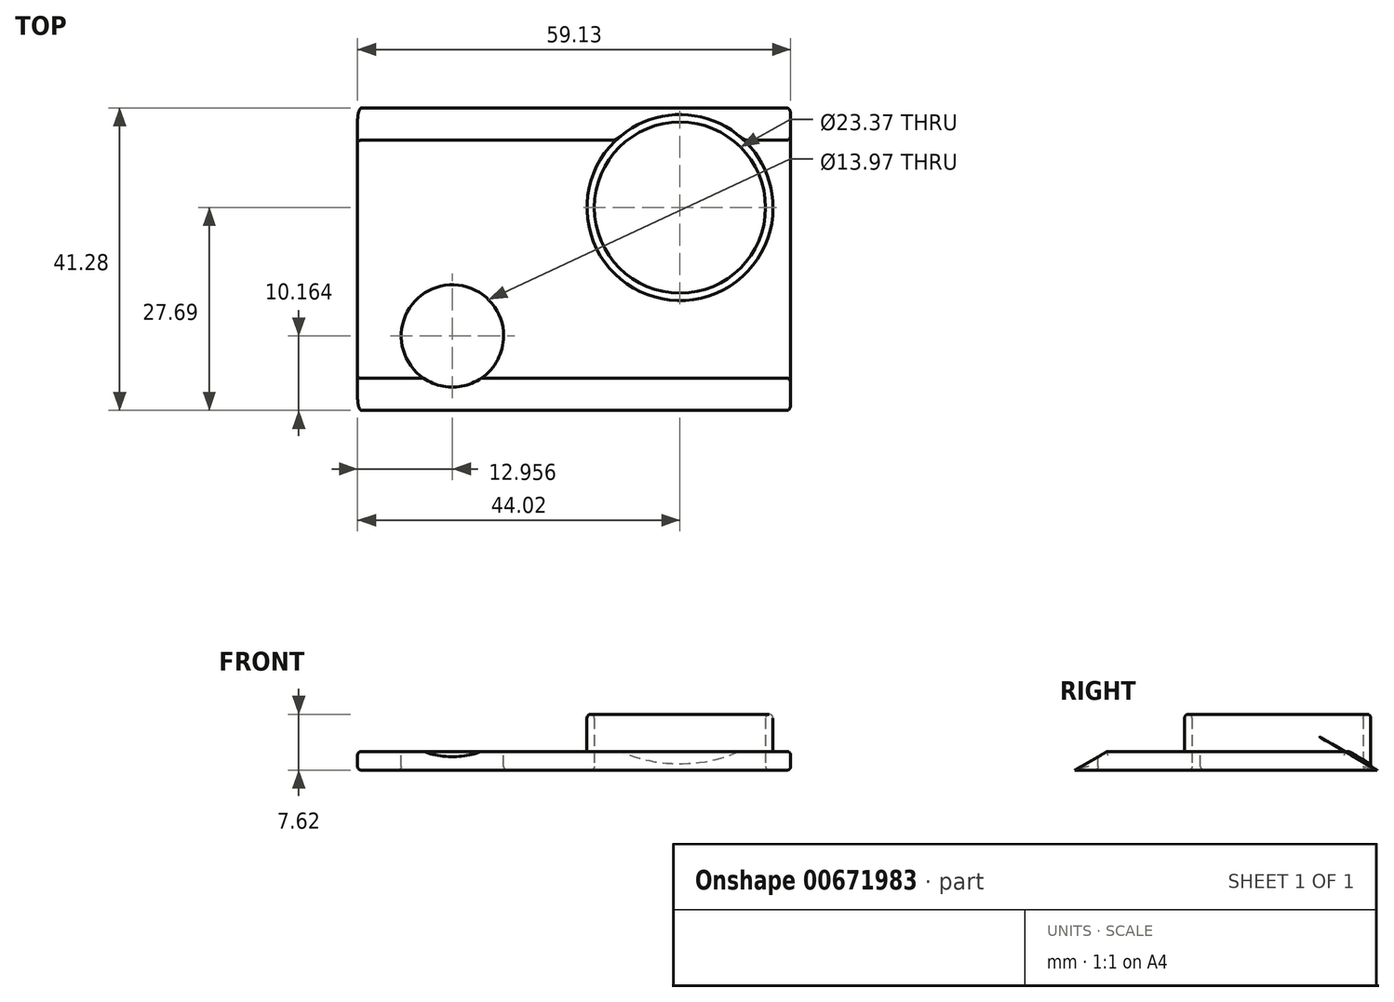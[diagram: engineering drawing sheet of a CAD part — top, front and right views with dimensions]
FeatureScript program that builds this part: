
annotation { "Feature Type Name" : "Feature", "Feature Type Description" : "" }
export const myFeature = defineFeature(function(context is Context, id is Id, definition is map)
    precondition{}
    {
        {
            var Q0;
            Q0=qCreatedBy(makeId("Top.planeOp"),FACE);
            var sketch = newSketch(context, id + "F0", { "sketchPlane" : qUnion([Q0])});
            skCircle(sketch, "E0", {"center": v(0, 0) * mm, "radius": 11.68 * mm});
            skCircle(sketch, "E1", {"center": v(0, 0) * mm, "radius": 12.7 * mm});
            skSolve(sketch);
        }
        {
            var Q0;
            Q0 = qSketchRegion(id + "F0", true);
            extrude(context, id + "F1", {"entities" : qUnion([Q0]), "depth" : 7.62 * mm, "offsetDistance" : 25.4 * mm});
        }
        {
            var Q0;
            Q0=makeQuery(id+"F1.opExtrude","CAP_FACE",FACE,{"disambiguationData":[OSD([sQuery(id+"F0.wireOp",EDGE,"E0"),sQuery(id+"F0.wireOp",EDGE,"E1")])],"isStart":true});
            var sketch = newSketch(context, id + "F2", { "sketchPlane" : qUnion([Q0])});
            skLineSegment(sketch, "E2.bottom", {"start": v(-44.02, -13.59) * mm, "end": v(15.11, -13.59) * mm});
            skLineSegment(sketch, "E2.top", {"start": v(-44.02, 27.69) * mm, "end": v(15.11, 27.69) * mm});
            skLineSegment(sketch, "E2.left", {"start": v(-44.02, -13.59) * mm, "end": v(-44.02, 27.69) * mm});
            skLineSegment(sketch, "E2.right", {"start": v(15.11, -13.59) * mm, "end": v(15.11, 27.69) * mm});
            skCircle(sketch, "E3.0", {"center": v(0, 0) * mm, "radius": 11.68 * mm});
            skSolve(sketch);
        }
        {
            var Q0;
            Q0 = qSketchRegion(id + "F2", true);
            extrude(context, id + "F3", {"entities" : qUnion([Q0]), "operationType" : NewBodyOperationType.ADD, "oppositeDirection" : true, "depth" : 2.54 * mm, "offsetDistance" : 25.4 * mm});
        }
        {
            var Q0;
            Q0=makeQuery(id+"F3.opExtrude","SWEPT_FACE",FACE,{"disambiguationData":[OSD([sQuery(id+"F2.wireOp",EDGE,"E2.right")])]});
            var sketch = newSketch(context, id + "F4", { "sketchPlane" : qUnion([Q0])});
            skLineSegment(sketch, "E4", {"start": v(-23.29, 2.54) * mm, "end": v(-27.69, 0) * mm});
            skLineSegment(sketch, "E5", {"start": v(-23.29, 2.54) * mm, "end": v(-27.69, 2.54) * mm});
            skLineSegment(sketch, "E6", {"start": v(-27.69, 0) * mm, "end": v(-27.69, 2.54) * mm});
            skLineSegment(sketch, "E7", {"start": v(9.19, 2.54) * mm, "end": v(13.59, 0) * mm});
            skLineSegment(sketch, "E8", {"start": v(9.19, 2.54) * mm, "end": v(13.59, 2.54) * mm});
            skLineSegment(sketch, "E9", {"start": v(13.59, 0) * mm, "end": v(13.59, 2.54) * mm});
            skSolve(sketch);
        }
        {
            var Q0;
            Q0 = qSketchRegion(id + "F4", true);
            extrude(context, id + "F5", {"entities" : qUnion([Q0]), "operationType" : NewBodyOperationType.REMOVE, "endBound" : BoundingType.THROUGH_ALL, "oppositeDirection" : true, "depth" : 25.4 * mm, "offsetDistance" : 25.4 * mm});
        }
        {
            var Q0;
            Q0=makeQuery(id+"F5.boolean.opBoolean","COPY",FACE,{"derivedFrom":makeQuery(id+"F5.opExtrude","SWEPT_FACE",FACE,{"disambiguationData":[OSD([sQuery(id+"F4.wireOp",EDGE,"E8")])]})});
            var sketch = newSketch(context, id + "F6", { "sketchPlane" : qUnion([Q0])});
            skArc(sketch, "E10.0", {"start": v(-8.77, -9.19) * mm, "mid": v(0, -12.7) * mm, "end": v(8.77, -9.19) * mm});
            skArc(sketch, "E10.1", {"start": v(7.22, -9.19) * mm, "mid": v(0, -11.68) * mm, "end": v(-7.22, -9.19) * mm});
            skLineSegment(sketch, "E10.2", {"start": v(7.22, -9.19) * mm, "end": v(8.77, -9.19) * mm});
            skLineSegment(sketch, "E10.3", {"start": v(-8.77, -9.19) * mm, "end": v(-7.22, -9.19) * mm});
            skSolve(sketch);
        }
        {
            var Q0;
            Q0 = qSketchRegion(id + "F6", true);
            var Q1;
            Q1=makeQuery(id+"F3.boolean.opBoolean","MERGE",FACE,{"derivedFrom":[makeQuery(id+"F1.opExtrude","CAP_FACE",FACE,{"disambiguationData":[OSD([sQuery(id+"F0.wireOp",EDGE,"E0"),sQuery(id+"F0.wireOp",EDGE,"E1")])],"isStart":true}),makeQuery(id+"F3.opExtrude","CAP_FACE",FACE,{"disambiguationData":[OSD([sQuery(id+"F2.wireOp",EDGE,"E2.bottom"),sQuery(id+"F2.wireOp",EDGE,"E2.top"),sQuery(id+"F2.wireOp",EDGE,"E2.left"),sQuery(id+"F2.wireOp",EDGE,"E2.right"),sQuery(id+"F2.wireOp",EDGE,"E3.0")])],"isStart":true})]});
            extrude(context, id + "F7", {"entities" : qUnion([Q0]), "operationType" : NewBodyOperationType.ADD, "endBound" : BoundingType.UP_TO_SURFACE, "depth" : 25.4 * mm, "endBoundEntityFace" : qUnion([Q1]), "offsetDistance" : 25.4 * mm});
        }
        {
            var Q0;
            Q0=makeQuery(id+"F3.opExtrude","CAP_EDGE",EDGE,{"disambiguationData":[OSD([sQuery(id+"F2.wireOp",EDGE,"E2.right")])],"isStart":false});
            var Q1;
            {var subQ0=sQuery(id+"F4.wireOp",EDGE,"E7");var subQ1=makeQuery(id+"F5.opExtrude","SWEPT_FACE",FACE,{"disambiguationData":[OSD([subQ0])]});var subQ2=sQuery(id+"F2.wireOp",EDGE,"E2.right");var subQ3=makeQuery(id+"F3.opExtrude","CAP_FACE",FACE,{"disambiguationData":[OSD([sQuery(id+"F2.wireOp",EDGE,"E2.bottom"),sQuery(id+"F2.wireOp",EDGE,"E2.top"),sQuery(id+"F2.wireOp",EDGE,"E2.left"),subQ2,sQuery(id+"F2.wireOp",EDGE,"E3.0")])],"isStart":false});var subQ4=sQuery(id+"F4.wireOp",EDGE,"E8");Q1=makeQuery(id+"F5.boolean.opBoolean","COPY",EDGE,{"disambiguationData":[topologyDisambiguationEdgeConnected([subQ3,subQ1]),TD([makeQuery(id+"F3.opExtrude","SWEPT_FACE",FACE,{"disambiguationData":[OSD([subQ2])]})])],"derivedFrom":makeQuery(id+"F5.opExtrude","SWEPT_EDGE",EDGE,{"disambiguationData":[OSD([subQ2,subQ0,subQ4])]})});}
            var Q2;
            Q2=makeQuery(id+"F7.boolean.opBoolean","INTERSECT",EDGE,{"derivedFrom":[makeQuery(id+"F5.boolean.opBoolean","COPY",FACE,{"derivedFrom":makeQuery(id+"F5.opExtrude","SWEPT_FACE",FACE,{"disambiguationData":[OSD([sQuery(id+"F4.wireOp",EDGE,"E7")])]})}),makeQuery(id+"F7.opExtrude","SWEPT_FACE",FACE,{"disambiguationData":[OSD([sQuery(id+"F6.wireOp",EDGE,"E10.0")])]})]});
            var Q3;
            {var subQ0=sQuery(id+"F4.wireOp",EDGE,"E7");var subQ1=makeQuery(id+"F5.opExtrude","SWEPT_FACE",FACE,{"disambiguationData":[OSD([subQ0])]});var subQ2=sQuery(id+"F2.wireOp",EDGE,"E2.left");var subQ3=sQuery(id+"F2.wireOp",EDGE,"E2.right");var subQ4=makeQuery(id+"F3.opExtrude","CAP_FACE",FACE,{"disambiguationData":[OSD([sQuery(id+"F2.wireOp",EDGE,"E2.bottom"),sQuery(id+"F2.wireOp",EDGE,"E2.top"),subQ2,subQ3,sQuery(id+"F2.wireOp",EDGE,"E3.0")])],"isStart":false});var subQ5=sQuery(id+"F4.wireOp",EDGE,"E8");Q3=makeQuery(id+"F5.boolean.opBoolean","COPY",EDGE,{"disambiguationData":[topologyDisambiguationEdgeConnected([subQ4,subQ1]),TD([makeQuery(id+"F3.opExtrude","SWEPT_FACE",FACE,{"disambiguationData":[OSD([subQ2])]})])],"derivedFrom":makeQuery(id+"F5.opExtrude","SWEPT_EDGE",EDGE,{"disambiguationData":[OSD([subQ3,subQ0,subQ5])]})});}
            var Q4;
            Q4=makeQuery(id+"F1.opExtrude","CAP_EDGE",EDGE,{"disambiguationData":[OSD([sQuery(id+"F0.wireOp",EDGE,"E1")])],"isStart":false});
            var Q5;
            Q5=makeQuery(id+"F1.opExtrude","CAP_EDGE",EDGE,{"disambiguationData":[OSD([sQuery(id+"F0.wireOp",EDGE,"E0")])],"isStart":false});
            var Q6;
            Q6=makeQuery(id+"F1.opExtrude","CAP_EDGE",EDGE,{"disambiguationData":[OSD([sQuery(id+"F0.wireOp",EDGE,"E0")])],"isStart":true});
            var Q7;
            Q7=makeQuery(id+"F5.boolean.opBoolean","COPY",EDGE,{"derivedFrom":makeQuery(id+"F5.opExtrude","CAP_EDGE",EDGE,{"disambiguationData":[OSD([sQuery(id+"F4.wireOp",EDGE,"E7")])],"isStart":true})});
            var Q8;
            Q8=makeQuery(id+"F3.opExtrude","CAP_EDGE",EDGE,{"disambiguationData":[OSD([sQuery(id+"F2.wireOp",EDGE,"E2.right")])],"isStart":true});
            var Q9;
            Q9=makeQuery(id+"F5.boolean.opBoolean","COPY",EDGE,{"derivedFrom":makeQuery(id+"F5.opExtrude","SWEPT_EDGE",EDGE,{"disambiguationData":[OSD([sQuery(id+"F2.wireOp",EDGE,"E2.right"),sQuery(id+"F4.wireOp",EDGE,"E4"),sQuery(id+"F4.wireOp",EDGE,"E5")])]})});
            var Q10;
            Q10=makeQuery(id+"F5.boolean.opBoolean","INTERSECT",EDGE,{"derivedFrom":[makeQuery(id+"F3.opExtrude","SWEPT_FACE",FACE,{"disambiguationData":[OSD([sQuery(id+"F2.wireOp",EDGE,"E2.left")])]}),makeQuery(id+"F5.opExtrude","SWEPT_FACE",FACE,{"disambiguationData":[OSD([sQuery(id+"F4.wireOp",EDGE,"E4")])]})]});
            var Q11;
            Q11=makeQuery(id+"F3.opExtrude","CAP_EDGE",EDGE,{"disambiguationData":[OSD([sQuery(id+"F2.wireOp",EDGE,"E2.left")])],"isStart":false});
            var Q12;
            Q12=makeQuery(id+"F5.boolean.opBoolean","INTERSECT",EDGE,{"derivedFrom":[makeQuery(id+"F3.opExtrude","SWEPT_FACE",FACE,{"disambiguationData":[OSD([sQuery(id+"F2.wireOp",EDGE,"E2.left")])]}),makeQuery(id+"F5.opExtrude","SWEPT_FACE",FACE,{"disambiguationData":[OSD([sQuery(id+"F4.wireOp",EDGE,"E7")])]})]});
            var Q13;
            Q13=makeQuery(id+"F3.opExtrude","CAP_EDGE",EDGE,{"disambiguationData":[OSD([sQuery(id+"F2.wireOp",EDGE,"E2.left")])],"isStart":true});
            var Q14;
            Q14=makeQuery(id+"F5.boolean.opBoolean","COPY",EDGE,{"derivedFrom":makeQuery(id+"F5.opExtrude","CAP_EDGE",EDGE,{"disambiguationData":[OSD([sQuery(id+"F4.wireOp",EDGE,"E4")])],"isStart":true})});
            fillet(context, id + "F8", {"entities" : qUnion([Q0, Q1, Q2, Q3, Q4, Q5, Q6, Q7, Q8, Q9, Q10, Q11, Q12, Q13, Q14]), "radius" : 0.5 * mm, "tangentPropagation" : true, "allowEdgeOverflow" : false});
        }
        {
            var Q0;
            Q0=makeQuery(id+"F3.opExtrude","CAP_FACE",FACE,{"disambiguationData":[OSD([sQuery(id+"F2.wireOp",EDGE,"E2.bottom"),sQuery(id+"F2.wireOp",EDGE,"E2.top"),sQuery(id+"F2.wireOp",EDGE,"E2.left"),sQuery(id+"F2.wireOp",EDGE,"E2.right"),sQuery(id+"F2.wireOp",EDGE,"E3.0")])],"isStart":false});
            var sketch = newSketch(context, id + "F9", { "sketchPlane" : qUnion([Q0])});
            skCircle(sketch, "E11", {"center": v(-31.06, -17.53) * mm, "radius": 6.99 * mm});
            skSolve(sketch);
        }
        {
            var Q0;
            Q0 = qSketchRegion(id + "F9", true);
            extrude(context, id + "F10", {"entities" : qUnion([Q0]), "operationType" : NewBodyOperationType.REMOVE, "oppositeDirection" : true, "depth" : 25.4 * mm, "offsetDistance" : 25.4 * mm});
        }
        {
            var Q0;
            {var subQ0=sQuery(id+"F4.wireOp",EDGE,"E5");var subQ1=sQuery(id+"F4.wireOp",EDGE,"E4");var subQ2=sQuery(id+"F2.wireOp",EDGE,"E2.right");Q0=makeQuery(id+"F10.boolean.opBoolean","INTERSECT",EDGE,{"disambiguationData":[OD(1.0)],"derivedFrom":[makeQuery(id+"F8.opFillet","BLEND_FACE",FACE,{"disambiguationData":[OSD([subQ2,subQ1,subQ0]),TDD([makeQuery(id+"F5.boolean.opBoolean","COPY",EDGE,{"derivedFrom":makeQuery(id+"F5.opExtrude","SWEPT_EDGE",EDGE,{"disambiguationData":[OSD([subQ2,subQ1,subQ0])]})})])]}),makeQuery(id+"F10.opExtrude","SWEPT_FACE",FACE,{"disambiguationData":[OSD([sQuery(id+"F9.wireOp",EDGE,"E11")])]})]});}
            var Q1;
            Q1=makeQuery(id+"F10.boolean.opBoolean","INTERSECT",EDGE,{"derivedFrom":[makeQuery(id+"F3.boolean.opBoolean","MERGE",FACE,{"derivedFrom":[makeQuery(id+"F1.opExtrude","CAP_FACE",FACE,{"disambiguationData":[OSD([sQuery(id+"F0.wireOp",EDGE,"E0"),sQuery(id+"F0.wireOp",EDGE,"E1")])],"isStart":true}),makeQuery(id+"F3.opExtrude","CAP_FACE",FACE,{"disambiguationData":[OSD([sQuery(id+"F2.wireOp",EDGE,"E2.bottom"),sQuery(id+"F2.wireOp",EDGE,"E2.top"),sQuery(id+"F2.wireOp",EDGE,"E2.left"),sQuery(id+"F2.wireOp",EDGE,"E2.right"),sQuery(id+"F2.wireOp",EDGE,"E3.0")])],"isStart":true})]}),makeQuery(id+"F10.opExtrude","SWEPT_FACE",FACE,{"disambiguationData":[OSD([sQuery(id+"F9.wireOp",EDGE,"E11")])]})]});
            fillet(context, id + "F11", {"entities" : qUnion([Q0, Q1]), "radius" : 0.5 * mm, "tangentPropagation" : true, "allowEdgeOverflow" : false});
        }
    });
